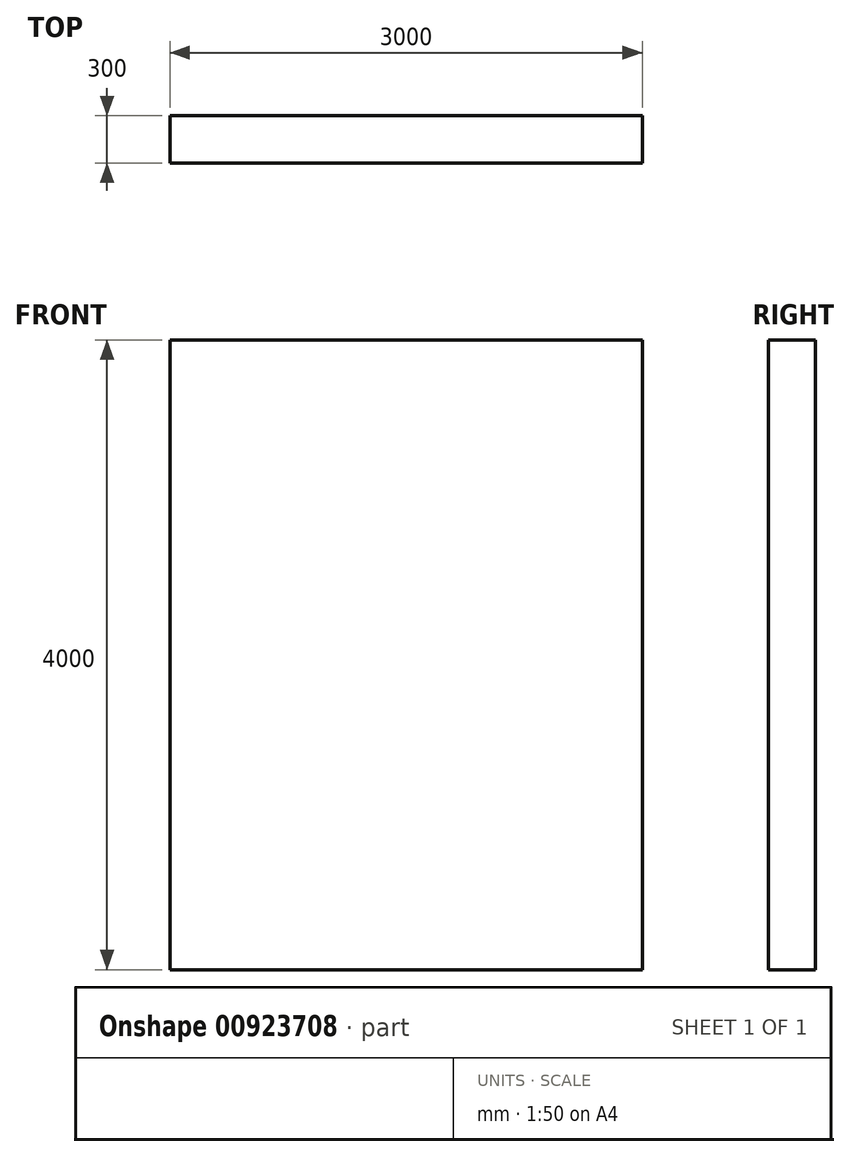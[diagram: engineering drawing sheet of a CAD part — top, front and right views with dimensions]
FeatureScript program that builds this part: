
annotation { "Feature Type Name" : "Feature", "Feature Type Description" : "" }
export const myFeature = defineFeature(function(context is Context, id is Id, definition is map)
    precondition{}
    {
        {
            var Q0;
            Q0=qCreatedBy(makeId("Top.planeOp"),FACE);
            var sketch = newSketch(context, id + "F0", { "sketchPlane" : qUnion([Q0])});
            skLineSegment(sketch, "E0.bottom", {"start": v(-1491.7, -79.16) * mm, "end": v(1508.3, -79.16) * mm});
            skLineSegment(sketch, "E0.top", {"start": v(-1491.7, -379.16) * mm, "end": v(1508.3, -379.16) * mm});
            skLineSegment(sketch, "E0.left", {"start": v(-1491.7, -79.16) * mm, "end": v(-1491.7, -379.16) * mm});
            skLineSegment(sketch, "E0.right", {"start": v(1508.3, -79.16) * mm, "end": v(1508.3, -379.16) * mm});
            skSolve(sketch);
        }
        {
            var Q0;
            Q0 = qSketchRegion(id + "F0", true);
            extrude(context, id + "F1", {"entities" : qUnion([Q0]), "depth" : 4000 * mm, "offsetDistance" : 25 * mm});
        }
    });
